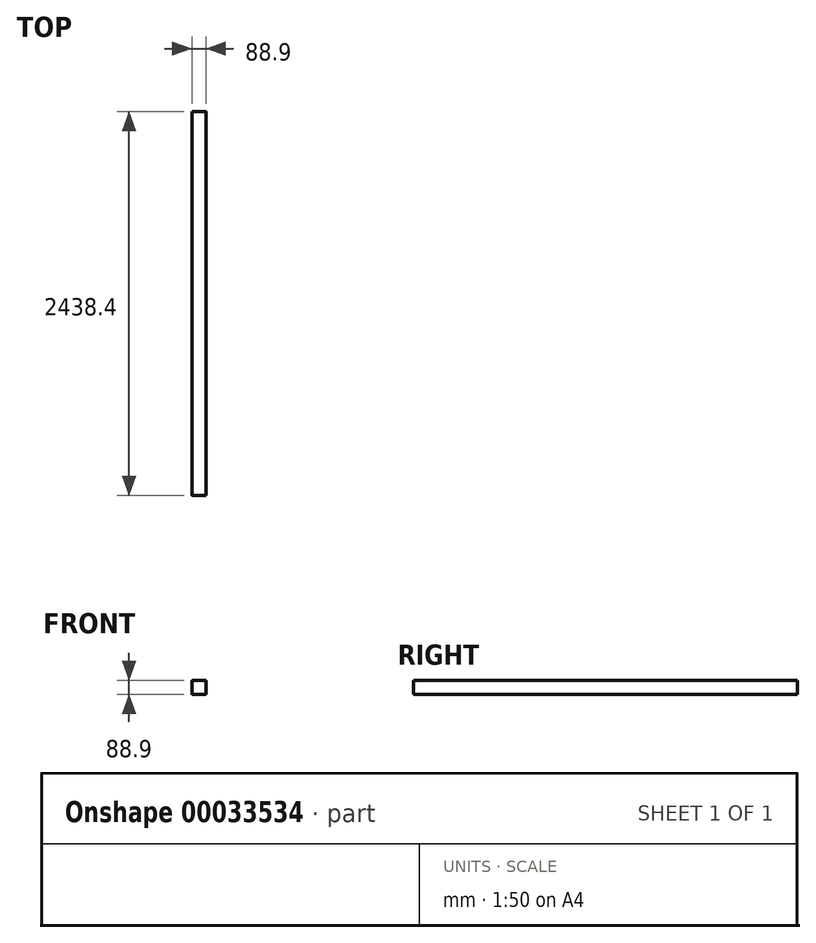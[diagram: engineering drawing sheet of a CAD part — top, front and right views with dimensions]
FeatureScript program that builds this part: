
annotation { "Feature Type Name" : "Feature", "Feature Type Description" : "" }
export const myFeature = defineFeature(function(context is Context, id is Id, definition is map)
    precondition{}
    {
        {
            var Q0;
            Q0=qCreatedBy(makeId("Front.planeOp"),FACE);
            var sketch = newSketch(context, id + "F0", { "sketchPlane" : qUnion([Q0])});
            skLineSegment(sketch, "E0.rect.bottom", {"start": v(41.28, 44.45) * mm, "end": v(-41.28, 44.45) * mm});
            skLineSegment(sketch, "E0.rect.top", {"start": v(41.28, -44.45) * mm, "end": v(-41.28, -44.45) * mm});
            skLineSegment(sketch, "E0.rect.left", {"start": v(44.45, 41.28) * mm, "end": v(44.45, -41.28) * mm});
            skLineSegment(sketch, "E0.rect.right", {"start": v(-44.45, 41.28) * mm, "end": v(-44.45, -41.28) * mm});
            skPoint(sketch, "E0.rect.middle", {"position": v(0, 0) * mm});
            skPoint(sketch, "E1.visualSharp", {"position": v(-44.45, 44.45) * mm});
            skArc(sketch, "E1.filletArc", {"start": v(-41.28, 44.45) * mm, "mid": v(-43.52, 43.52) * mm, "end": v(-44.45, 41.28) * mm});
            skPoint(sketch, "E2.visualSharp", {"position": v(44.45, 44.45) * mm});
            skArc(sketch, "E2.filletArc", {"start": v(44.45, 41.28) * mm, "mid": v(43.52, 43.52) * mm, "end": v(41.28, 44.45) * mm});
            skPoint(sketch, "E3.visualSharp", {"position": v(44.45, -44.45) * mm});
            skArc(sketch, "E3.filletArc", {"start": v(41.28, -44.45) * mm, "mid": v(43.52, -43.52) * mm, "end": v(44.45, -41.28) * mm});
            skPoint(sketch, "E4.visualSharp", {"position": v(-44.45, -44.45) * mm});
            skArc(sketch, "E4.filletArc", {"start": v(-44.45, -41.28) * mm, "mid": v(-43.52, -43.52) * mm, "end": v(-41.28, -44.45) * mm});
            skSolve(sketch);
        }
        {
            var Q0;
            Q0=makeQuery(id+"F0.imprint","IMPRINT",FACE,{"disambiguationData":[TD([[makeQuery(id+"F0.imprint","IMPRINT",EDGE,{"derivedFrom":sQuery(id+"F0.wireOp",EDGE,"E0.rect.bottom")}),1.0]])]});
            extrude(context, id + "F1", {"entities" : qUnion([Q0]), "oppositeDirection" : true, "depth" : 2438.4 * mm});
        }
    });
